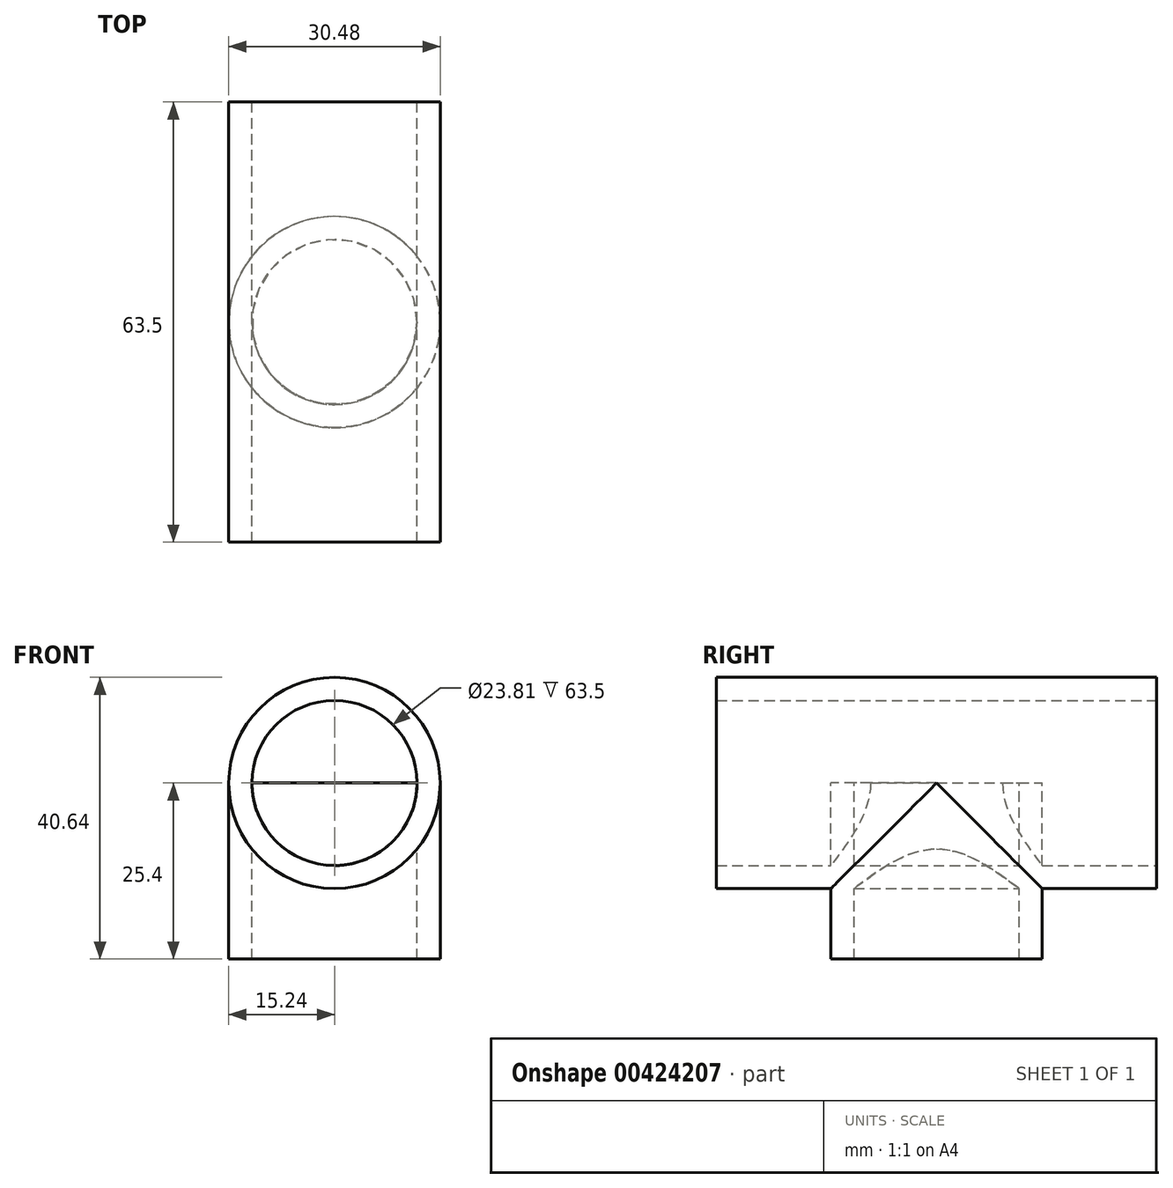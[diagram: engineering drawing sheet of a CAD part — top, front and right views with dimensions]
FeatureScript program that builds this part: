
annotation { "Feature Type Name" : "Feature", "Feature Type Description" : "" }
export const myFeature = defineFeature(function(context is Context, id is Id, definition is map)
    precondition{}
    {
        {
            var Q0;
            Q0=qCreatedBy(makeId("Front.planeOp"),FACE);
            var sketch = newSketch(context, id + "F0", { "sketchPlane" : qUnion([Q0])});
            skCircle(sketch, "E0", {"center": v(0, 0) * mm, "radius": 15.24 * mm});
            skCircle(sketch, "E1", {"center": v(0, 0) * mm, "radius": 11.9 * mm});
            skSolve(sketch);
        }
        {
            var Q0;
            Q0=makeQuery(id+"F0.imprint","IMPRINT",FACE,{"disambiguationData":[TD([[makeQuery(id+"F0.imprint","IMPRINT",EDGE,{"derivedFrom":sQuery(id+"F0.wireOp",EDGE,"E0")}),1.0]])]});
            extrude(context, id + "F1", {"entities" : qUnion([Q0]), "endBound" : BoundingType.SYMMETRIC, "depth" : 63.5 * mm});
        }
        {
            var Q0;
            Q0=qCreatedBy(makeId("Top.planeOp"),FACE);
            var sketch = newSketch(context, id + "F2", { "sketchPlane" : qUnion([Q0])});
            skCircle(sketch, "E2", {"center": v(0, 0) * mm, "radius": 15.24 * mm});
            skCircle(sketch, "E3", {"center": v(0, 0) * mm, "radius": 11.9 * mm});
            skSolve(sketch);
        }
        {
            var Q0;
            Q0=qSketchRegion(id+"F2",true);
            extrude(context, id + "F3", {"entities" : qUnion([Q0]), "operationType" : NewBodyOperationType.ADD, "oppositeDirection" : true, "depth" : 25.4 * mm});
        }
    });
